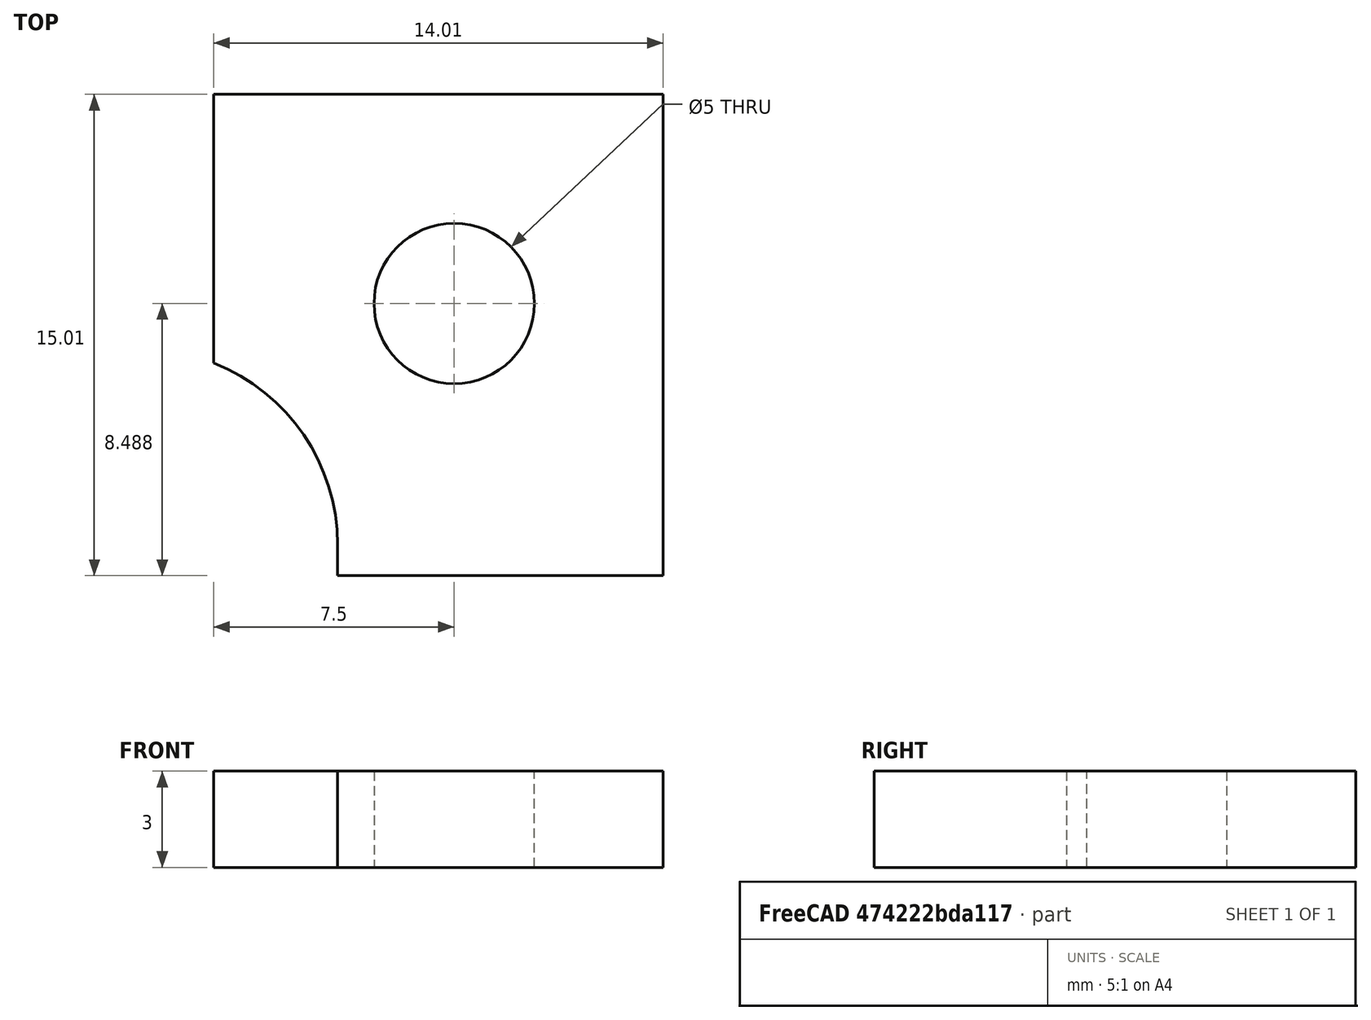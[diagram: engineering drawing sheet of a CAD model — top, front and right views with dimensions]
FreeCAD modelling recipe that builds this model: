
FCSTD DOCUMENT  (FreeCAD 0.18R16110 (Git))
Label: handlecurve
License: All rights reserved
LicenseURL: http://en.wikipedia.org/wiki/All_rights_reserved
objects: Sketcher::SketchObject×1, Part::Extrusion×1
note: 2 computed .brp shape members not serialized (recipe doc carries the construction recipe); baked Part::Feature solids carry a one-line shape summary decoded from their .brp

FEATURE [Sketcher::SketchObject] Sketch
  sketch-geometry (12):
    g0: LineSegment StartX=-7.49541 StartY=14.0405 StartZ=0 EndX=6.50881 EndY=14.0405 EndZ=0
    g1: LineSegment StartX=6.50881 StartY=14.0405 StartZ=0 EndX=6.50881 EndY=0 EndZ=0
    g2: LineSegment StartX=-7.49541 StartY=5.6558 StartZ=0 EndX=-7.49541 EndY=14.0405 EndZ=0
    g3: ArcOfCircle CenterX=-9.70954 CenterY=0 CenterZ=0 NormalX=0 NormalY=0 NormalZ=1 AngleXU=0 Radius=6.07375 StartAngle=0 EndAngle=1.19766
    g4: Circle CenterX=0 CenterY=7.51777 CenterZ=0 NormalX=0 NormalY=0 NormalZ=1 AngleXU=0 Radius=2.5
    g5: LineSegment [constr] StartX=6.50881 StartY=14.0405 StartZ=0 EndX=6.48741 EndY=15.0035 EndZ=0
    g6: LineSegment [constr] StartX=6.50881 StartY=15.5091 StartZ=0 EndX=6.50053 EndY=15.5091 EndZ=0
    g7: LineSegment [constr] StartX=4.95539 StartY=-0.974619 StartZ=0 EndX=4.95539 EndY=-1.03653 EndZ=0
    g8: LineSegment StartX=6.50881 StartY=0 StartZ=0 EndX=6.50881 EndY=-0.974619 EndZ=0
    g9: LineSegment StartX=6.50881 StartY=-0.974619 StartZ=0 EndX=-3.63579 EndY=-0.974619 EndZ=0
    g10: LineSegment StartX=-3.63579 StartY=0 StartZ=0 EndX=-3.63579 EndY=-0.974619 EndZ=0
    g11: LineSegment [constr] StartX=3.17723 StartY=14.0405 StartZ=0 EndX=3.17723 EndY=14.0262 EndZ=0
  constraints (24):
    c: Coincident(g0,g1)
    c: PointOnObject(g1,g-1)
    c: Vertical(g1)
    c: PointOnObject(g3,g-1)
    c: Coincident(g2,g0)
    c: Vertical(g2)
    c: PointOnObject(g3,g-1)
    c: Coincident(g3,g2)
    c: PointOnObject(g4,g-2)
    c: Radius(g4) = 2.5
    c: Coincident(g5,g0)
    c: Horizontal(g6)
    c: Horizontal(g0)
    c: Vertical(g7)
    c: Coincident(g8,g1)
    c: Vertical(g8)
    c: Coincident(g9,g8)
    c: Horizontal(g9)
    c: Coincident(g10,g3)
    c: Coincident(g10,g9)
    c: Vertical(g10)
    c: PointOnObject(g7,g9)
    c: PointOnObject(g11,g0)
    c: Vertical(g11)
FEATURE [Part::Extrusion] Extrude
  Base = -> Sketch
  Dir = (0,0,1)
  DirMode = 2
  FaceMakerClass = Part::FaceMakerBullseye
  LengthFwd = 3
  LengthRev = 0
  Solid = true
  Symmetric = false
